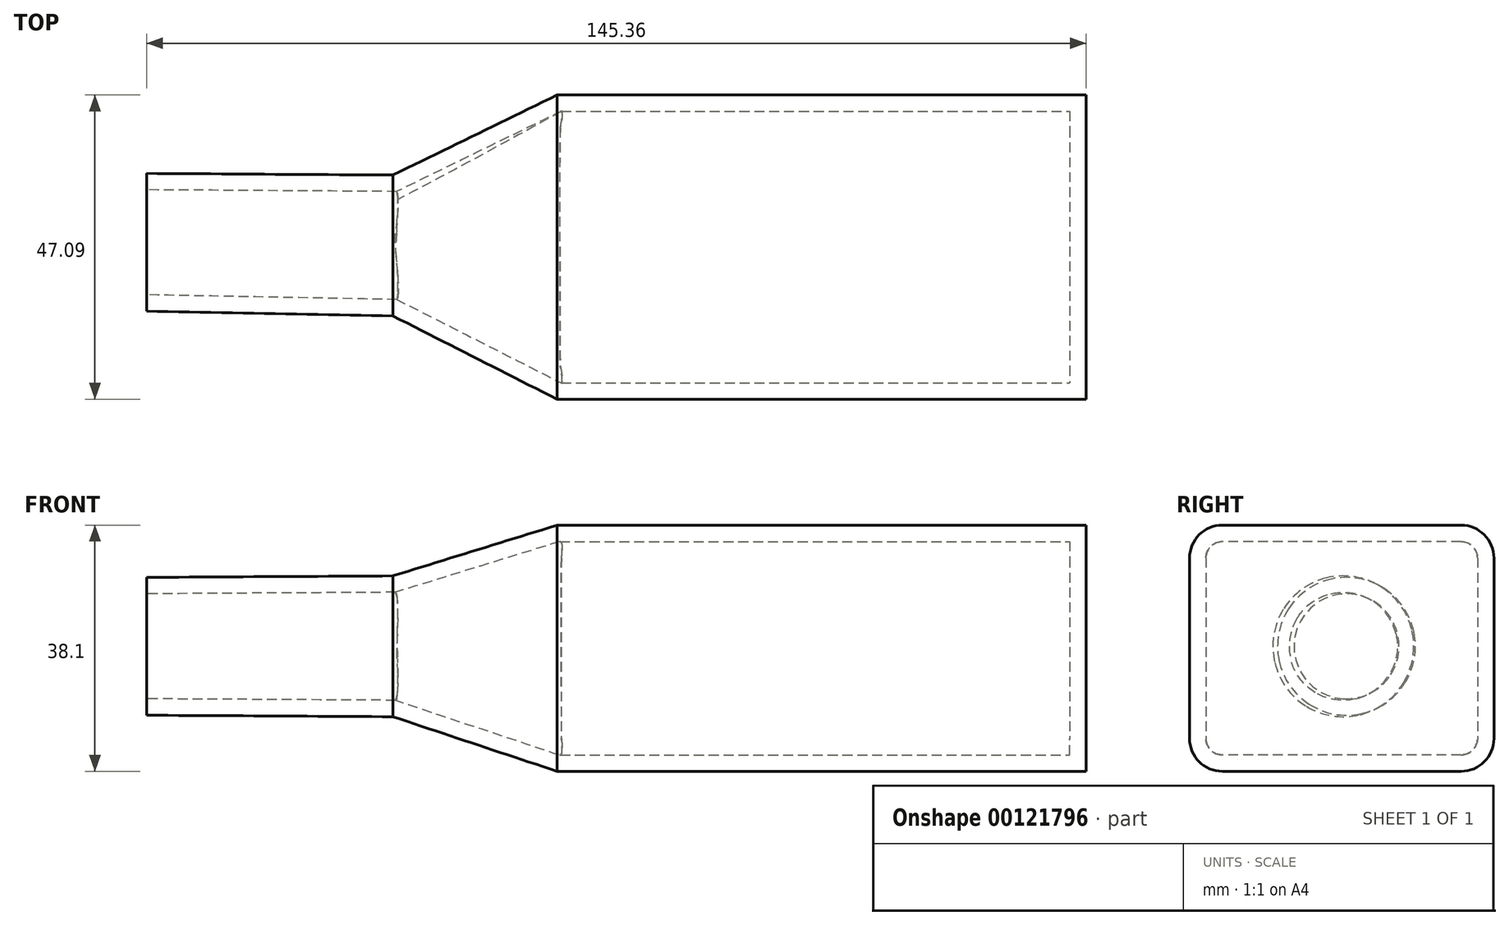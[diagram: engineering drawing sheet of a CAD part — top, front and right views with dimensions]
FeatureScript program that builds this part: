
annotation { "Feature Type Name" : "Feature", "Feature Type Description" : "" }
export const myFeature = defineFeature(function(context is Context, id is Id, definition is map)
    precondition{}
    {
        {
            var Q0;
            Q0=qCreatedBy(makeId("Top.planeOp"),FACE);
            var sketch = newSketch(context, id + "F0", { "sketchPlane" : qUnion([Q0])});
            skLineSegment(sketch, "E0.bottom", {"start": v(-12.33, 28.97) * mm, "end": v(69.53, 28.97) * mm});
            skLineSegment(sketch, "E0.top", {"start": v(-12.33, -18.12) * mm, "end": v(69.53, -18.12) * mm});
            skLineSegment(sketch, "E0.left", {"start": v(-12.33, 28.97) * mm, "end": v(-12.33, -18.12) * mm});
            skLineSegment(sketch, "E0.right", {"start": v(69.53, 28.97) * mm, "end": v(69.53, -18.12) * mm});
            skSolve(sketch);
        }
        {
            var Q0;
            Q0=makeQuery(id+"F0.imprint","IMPRINT",FACE,{"disambiguationData":[TD([[makeQuery(id+"F0.imprint","IMPRINT",EDGE,{"derivedFrom":sQuery(id+"F0.wireOp",EDGE,"E0.bottom")}),-1.0]])]});
            extrude(context, id + "F1", {"entities" : qUnion([Q0]), "depth" : 38.1 * mm});
        }
        {
            var Q0;
            Q0=makeQuery(id+"F1.opExtrude","CAP_EDGE",EDGE,{"disambiguationData":[OSD([sQuery(id+"F0.wireOp",EDGE,"E0.bottom")])],"isStart":false});
            var Q1;
            Q1=makeQuery(id+"F1.opExtrude","CAP_EDGE",EDGE,{"disambiguationData":[OSD([sQuery(id+"F0.wireOp",EDGE,"E0.top")])],"isStart":false});
            var Q2;
            Q2=makeQuery(id+"F1.opExtrude","CAP_EDGE",EDGE,{"disambiguationData":[OSD([sQuery(id+"F0.wireOp",EDGE,"E0.bottom")])],"isStart":true});
            var Q3;
            Q3=makeQuery(id+"F1.opExtrude","CAP_EDGE",EDGE,{"disambiguationData":[OSD([sQuery(id+"F0.wireOp",EDGE,"E0.top")])],"isStart":true});
            fillet(context, id + "F2", {"entities" : qUnion([Q0, Q1, Q2, Q3]), "radius" : 5.08 * mm, "tangentPropagation" : true, "allowEdgeOverflow" : false});
        }
        {
            var Q0;
            Q0=makeQuery(id+"F1.opExtrude","SWEPT_FACE",FACE,{"disambiguationData":[OSD([sQuery(id+"F0.wireOp",EDGE,"E0.left")])]});
            cPlane(context, id + "F3", {"entities" : qUnion([Q0]), "cplaneType" : CPlaneType.OFFSET, "offset" : 25.4 * mm, "width" : 152.4 * mm, "height" : 152.4 * mm});
        }
        {
            var Q0;
            Q0=qCreatedBy(id+"F3.planeOp",FACE);
            var sketch = newSketch(context, id + "F4", { "sketchPlane" : qUnion([Q0])});
            skCircle(sketch, "E1", {"center": v(-5.67, 19.36) * mm, "radius": 10.9 * mm});
            skSolve(sketch);
        }
        {
            var Q1;
            Q1=makeQuery(id+"F1.opExtrude","SWEPT_FACE",FACE,{"disambiguationData":[OSD([sQuery(id+"F0.wireOp",EDGE,"E0.left")])]});
            var Q2;
            Q2=makeQuery(id+"F4.imprint","IMPRINT",FACE,{"disambiguationData":[TD([[makeQuery(id+"F4.imprint","IMPRINT",EDGE,{"derivedFrom":sQuery(id+"F4.wireOp",EDGE,"E1")}),1.0]])]});
            loft(context, id + "F5", {"operationType" : NewBodyOperationType.ADD, "sheetProfilesArray" : [{ "sheetProfileEntities" : qUnion([Q1]) }, { "sheetProfileEntities" : qUnion([Q2]) }]});
        }
        {
            var Q0;
            Q0=makeQuery(id+"F5.opLoft","CAP_FACE",FACE,{"disambiguationData":[OSD([makeQuery(id+"F4.imprint","IMPRINT",FACE,{"disambiguationData":[TD([[makeQuery(id+"F4.imprint","IMPRINT",EDGE,{"derivedFrom":sQuery(id+"F4.wireOp",EDGE,"E1")}),1.0]])]})])],"isStart":true});
            cPlane(context, id + "F6", {"entities" : qUnion([Q0]), "cplaneType" : CPlaneType.OFFSET, "offset" : 38.1 * mm, "width" : 152.4 * mm, "height" : 152.4 * mm});
        }
        {
            var Q0;
            Q0=qCreatedBy(id+"F6.planeOp",FACE);
            var sketch = newSketch(context, id + "F7", { "sketchPlane" : qUnion([Q0])});
            skCircle(sketch, "E2", {"center": v(-6.16, 19.36) * mm, "radius": 10.67 * mm});
            skSolve(sketch);
        }
        {
            var Q1;
            Q1=makeQuery(id+"F7.imprint","IMPRINT",FACE,{"disambiguationData":[TD([[makeQuery(id+"F7.imprint","IMPRINT",EDGE,{"derivedFrom":sQuery(id+"F7.wireOp",EDGE,"E2")}),1.0]])]});
            var Q2;
            Q2=makeQuery(id+"F5.opLoft","CAP_FACE",FACE,{"disambiguationData":[OSD([makeQuery(id+"F4.imprint","IMPRINT",FACE,{"disambiguationData":[TD([[makeQuery(id+"F4.imprint","IMPRINT",EDGE,{"derivedFrom":sQuery(id+"F4.wireOp",EDGE,"E1")}),1.0]])]})])],"isStart":true});
            loft(context, id + "F8", {"operationType" : NewBodyOperationType.ADD, "sheetProfilesArray" : [{ "sheetProfileEntities" : qUnion([Q1]) }, { "sheetProfileEntities" : qUnion([Q2]) }]});
        }
        {
            var Q0;
            Q0=makeQuery(id+"F8.opLoft","CAP_FACE",FACE,{"disambiguationData":[OSD([makeQuery(id+"F7.imprint","IMPRINT",FACE,{"disambiguationData":[TD([[makeQuery(id+"F7.imprint","IMPRINT",EDGE,{"derivedFrom":sQuery(id+"F7.wireOp",EDGE,"E2")}),1.0]])]})])],"isStart":true});
            shell(context, id + "F9", {"entities" : qUnion([Q0]), "thickness" : 2.54 * mm});
        }
    });
